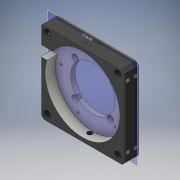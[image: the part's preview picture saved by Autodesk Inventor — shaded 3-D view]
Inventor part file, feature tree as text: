
AUTODESK INVENTOR PART (.ipt)
format: ipt  version: 2016 (Build 200138000, 138)  size: 1,113,088 bytes
history: native  units: in
note: dims shown in document units (in); Inventor stores cm internally (conversion verified against a paired STEP export)
features: other x9, projected_geometry x8, sketch x6, extrude x4, hole x2, pattern_circular x2, plane x1
ambient origin geometry x8: Origin, YZ Plane, XZ Plane, XY Plane, X Axis, Y Axis, Z Axis, Center Point
bodies: Solid1 (feature_tree), Solid2 (feature_tree), Solid3 (feature_tree), Solid4 (feature_tree), Solid5 (feature_tree), Solid6 (feature_tree), Solid7 (feature_tree), Solid8 (feature_tree), Solid9 (feature_tree)
feature tree (32):
  plane  "Work Plane3"
  extrude  "Extrusion1"  Depth=2.5in
  extrude  "Extrusion2"  Depth=1.0in TaperAngle=0.0deg
  extrude  "Extrusion3"  Depth=1.0in TaperAngle=0.0deg
  hole  "Hole1"  [1 undecoded]
  pattern_circular  "Circular Pattern1"  [2 undecoded]
  hole  "Hole2"  [1 undecoded]
  pattern_circular  "Circular Pattern2"  [2 undecoded]
  extrude  "Extrusion4"  Depth=0.35in TaperAngle=0.0deg
  sketch  "Sketch1"  dims[d0=1.0in d1=0.0in d2=2.5in]
  sketch  "Sketch2"  dims[d5=-0.1575in d6=1.0in d7=0.0in]
  projected_geometry  "Projected Loop1"
  sketch  "Sketch3"  dims[d8=1.4932in d9=1.0in d10=0.0in]
  projected_geometry  "Projected Loop2"
  projected_geometry  "Projected Loop3"
  sketch  "Sketch4"  dims[d11=1.6703in]
  projected_geometry  "Projected Loop4"
  projected_geometry  "Projected Loop5"
  sketch  "Sketch5"  dims[d12=0.129in d13=0.75in d14=0.219in d15=0.112in d16=0.5635in d17=1.0in d18=0.8108in d19=1.5748in d20=360.0deg]
  projected_geometry  "Projected Loop6"
  projected_geometry  "Projected Loop7"
  sketch  "Sketch6"  dims[d22=2.12in d23=1.2987in d24=0.067in d25=0.172in d26=0.188in d27=0.086in d28=0.5635in d29=0.261in d30=0.8108in d31=1.9685in d32=360.0deg d34=0.35in d35=1.0in d36=0.0in]
  projected_geometry  "Projected Loop8"
  other  "13107-001-1-solid1"
  other  "SS4S019-1-1-solid1"
  other  "SS4S019-1-2-solid1"
  other  "SS4S019-1-3-solid1"
  other  "SS4S019-1-4-solid1"
  other  "SS4S019-1-5-solid1"
  other  "SS4S019-1-6-solid1"
  other  "SS4S019-1-7-solid1"
  other  "SS4S019-1-8-solid1"
note: 6 required parameter values undecoded (feature->parameter linkage not recoverable at this tier; creation-order binding heuristic only, values carry confidence <= 0.55)
